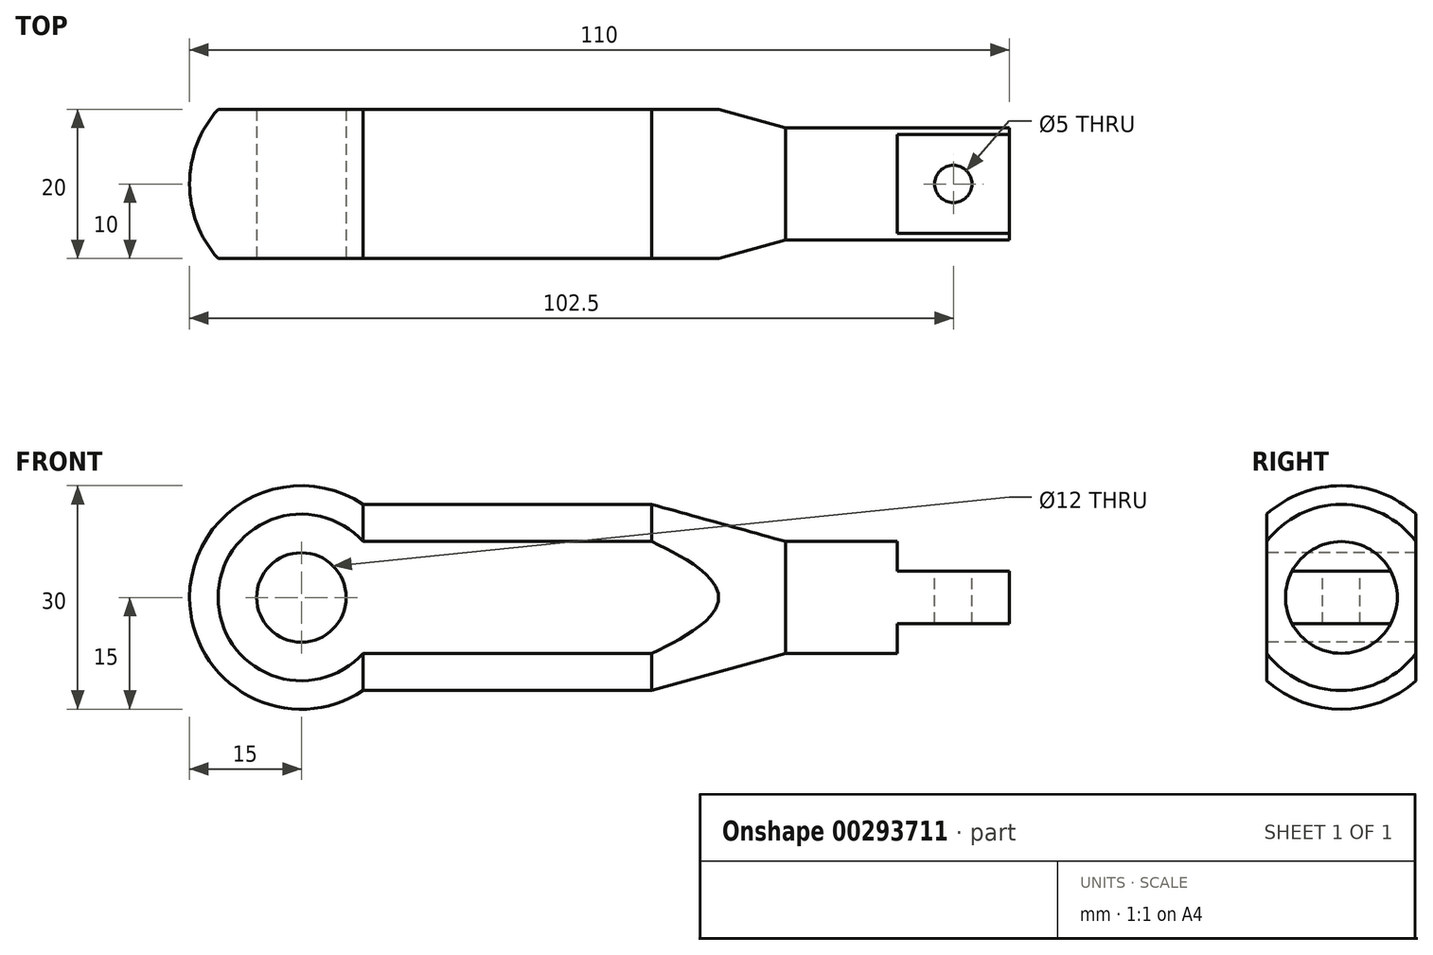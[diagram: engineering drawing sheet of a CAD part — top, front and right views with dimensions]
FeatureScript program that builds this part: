
annotation { "Feature Type Name" : "Feature", "Feature Type Description" : "" }
export const myFeature = defineFeature(function(context is Context, id is Id, definition is map)
    precondition{}
    {
        {
            var Q0;
            Q0=qCreatedBy(makeId("Front.planeOp"),FACE);
            var sketch = newSketch(context, id + "F0", { "sketchPlane" : qUnion([Q0])});
            skLineSegment(sketch, "E0", {"start": v(0, 0) * mm, "end": v(124.44, 0) * mm, "construction": true});
            skArc(sketch, "E1", {"start": v(8.3, 12.5) * mm, "mid": v(-7.1, 13.22) * mm, "end": v(-15, 0) * mm});
            skLineSegment(sketch, "E2", {"start": v(8.3, 12.5) * mm, "end": v(47, 12.5) * mm});
            skLineSegment(sketch, "E3", {"start": v(47, 12.5) * mm, "end": v(65, 7.5) * mm});
            skLineSegment(sketch, "E4", {"start": v(65, 7.5) * mm, "end": v(95, 7.5) * mm});
            skLineSegment(sketch, "E5", {"start": v(95, 7.5) * mm, "end": v(95, 0) * mm});
            skLineSegment(sketch, "E6", {"start": v(-15, 0) * mm, "end": v(95, 0) * mm});
            skSolve(sketch);
        }
        {
            var Q0;
            Q0=makeQuery(id+"F0.imprint","IMPRINT",FACE,{"disambiguationData":[TD([[makeQuery(id+"F0.imprint","IMPRINT",EDGE,{"derivedFrom":sQuery(id+"F0.wireOp",EDGE,"E1")}),1.0]])]});
            var Q1;
            Q1=sQuery(id+"F0.wireOp",EDGE,"E0");
            revolve(context, id + "F1", {"entities" : qUnion([Q0]), "axis" : qUnion([Q1]), "revolveType" : RevolveType.FULL});
        }
        {
            var Q0;
            Q0=qCreatedBy(makeId("Front.planeOp"),FACE);
            var sketch = newSketch(context, id + "F2", { "sketchPlane" : qUnion([Q0])});
            skLineSegment(sketch, "E7.top", {"start": v(80, 3.5) * mm, "end": v(95, 3.5) * mm});
            skLineSegment(sketch, "E7.left", {"start": v(80, 7.5) * mm, "end": v(80, 3.5) * mm});
            skLineSegment(sketch, "E8.0", {"start": v(80, 7.5) * mm, "end": v(95, 7.5) * mm});
            skPoint(sketch, "E9.orphan", {"position": v(65, 7.5) * mm});
            skLineSegment(sketch, "E10", {"start": v(95, 7.5) * mm, "end": v(95, 3.5) * mm});
            skLineSegment(sketch, "E11", {"start": v(75.68, 0) * mm, "end": v(97.4, 0) * mm, "construction": true});
            skLineSegment(sketch, "E12.MirrorCS", {"start": v(80, -3.5) * mm, "end": v(95, -3.5) * mm});
            skLineSegment(sketch, "E13.MirrorCS", {"start": v(80, -7.5) * mm, "end": v(95, -7.5) * mm});
            skLineSegment(sketch, "E14.MirrorCS", {"start": v(80, -7.5) * mm, "end": v(80, -3.5) * mm});
            skLineSegment(sketch, "E15.MirrorCS", {"start": v(95, -7.5) * mm, "end": v(95, -3.5) * mm});
            skSolve(sketch);
        }
        {
            var Q0;
            Q0 = qSketchRegion(id + "F2", true);
            extrude(context, id + "F3", {"entities" : qUnion([Q0]), "operationType" : NewBodyOperationType.REMOVE, "endBound" : BoundingType.THROUGH_ALL, "oppositeDirection" : true, "depth" : 25 * mm, "hasSecondDirection" : true, "secondDirectionBound" : SecondDirectionBoundingType.THROUGH_ALL, "secondDirectionOppositeDirection" : false, "secondDirectionDepth" : 25 * mm});
        }
        {
            var Q0;
            Q0=makeQuery(id+"F1.opRevolve","SWEPT_FACE",FACE,{"disambiguationData":[OSD([sQuery(id+"F0.wireOp",EDGE,"E5")])]});
            var sketch = newSketch(context, id + "F4", { "sketchPlane" : qUnion([Q0])});
            skLineSegment(sketch, "E16", {"start": v(-10, 11.18) * mm, "end": v(-10, -11.18) * mm});
            skArc(sketch, "E17", {"start": v(-10, 11.18) * mm, "mid": v(-15, 0) * mm, "end": v(-10, -11.18) * mm});
            skPoint(sketch, "E18.endSnap0", {"position": v(0, -3.5) * mm});
            skLineSegment(sketch, "E19", {"start": v(0, 0) * mm, "end": v(0, 17.37) * mm, "construction": true});
            skLineSegment(sketch, "E20", {"start": v(10, 11.18) * mm, "end": v(10, -11.18) * mm});
            skArc(sketch, "E21.trimOffspring", {"start": v(10, -11.18) * mm, "mid": v(15, 0) * mm, "end": v(10, 11.18) * mm});
            skSolve(sketch);
        }
        {
            var Q0;
            Q0 = qSketchRegion(id + "F4", true);
            extrude(context, id + "F5", {"entities" : qUnion([Q0]), "operationType" : NewBodyOperationType.REMOVE, "endBound" : BoundingType.THROUGH_ALL, "oppositeDirection" : true, "depth" : 25 * mm});
        }
        {
            var Q0;
            Q0=makeQuery(id+"F5.boolean.opBoolean","COPY",FACE,{"derivedFrom":makeQuery(id+"F5.opExtrude","SWEPT_FACE",FACE,{"disambiguationData":[OSD([sQuery(id+"F4.wireOp",EDGE,"E16")])]})});
            var sketch = newSketch(context, id + "F6", { "sketchPlane" : qUnion([Q0])});
            skCircle(sketch, "E22", {"center": v(0, 0) * mm, "radius": 6 * mm});
            skSolve(sketch);
        }
        {
            var Q0;
            Q0 = qSketchRegion(id + "F6", true);
            extrude(context, id + "F7", {"entities" : qUnion([Q0]), "operationType" : NewBodyOperationType.REMOVE, "endBound" : BoundingType.THROUGH_ALL, "oppositeDirection" : true, "depth" : 25 * mm});
        }
        {
            var Q0;
            Q0=makeQuery(id+"F3.boolean.opBoolean","COPY",FACE,{"derivedFrom":makeQuery(id+"F3.opExtrude","SWEPT_FACE",FACE,{"disambiguationData":[OSD([sQuery(id+"F2.wireOp",EDGE,"E7.top")])]})});
            var sketch = newSketch(context, id + "F8", { "sketchPlane" : qUnion([Q0])});
            skCircle(sketch, "E23", {"center": v(87.5, 0) * mm, "radius": 2.5 * mm});
            skSolve(sketch);
        }
        {
            var Q0;
            Q0 = qSketchRegion(id + "F8", true);
            extrude(context, id + "F9", {"entities" : qUnion([Q0]), "operationType" : NewBodyOperationType.REMOVE, "endBound" : BoundingType.THROUGH_ALL, "oppositeDirection" : true, "depth" : 25 * mm});
        }
    });
